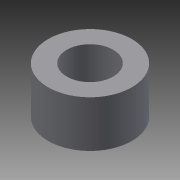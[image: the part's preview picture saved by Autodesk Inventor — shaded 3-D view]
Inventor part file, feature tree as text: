
AUTODESK INVENTOR PART (.ipt)
format: ipt  version: 2015 (Build 190159000, 159)  size: 74,752 bytes
history: native  units: in
note: dims shown in document units (in); Inventor stores cm internally (conversion verified against a paired STEP export)
features: extrude x1, sketch x1
ambient origin geometry x8: Origin, YZ Plane, XZ Plane, XY Plane, X Axis, Y Axis, Z Axis, Center Point
bodies: Solid1 (feature_tree)
feature tree (2):
  extrude  "Extrusion1"  Depth=0.25in
  sketch  "Sketch1"  dims[d0=0.25in d1=0.45in d2=0.25in d3=0.0in]
